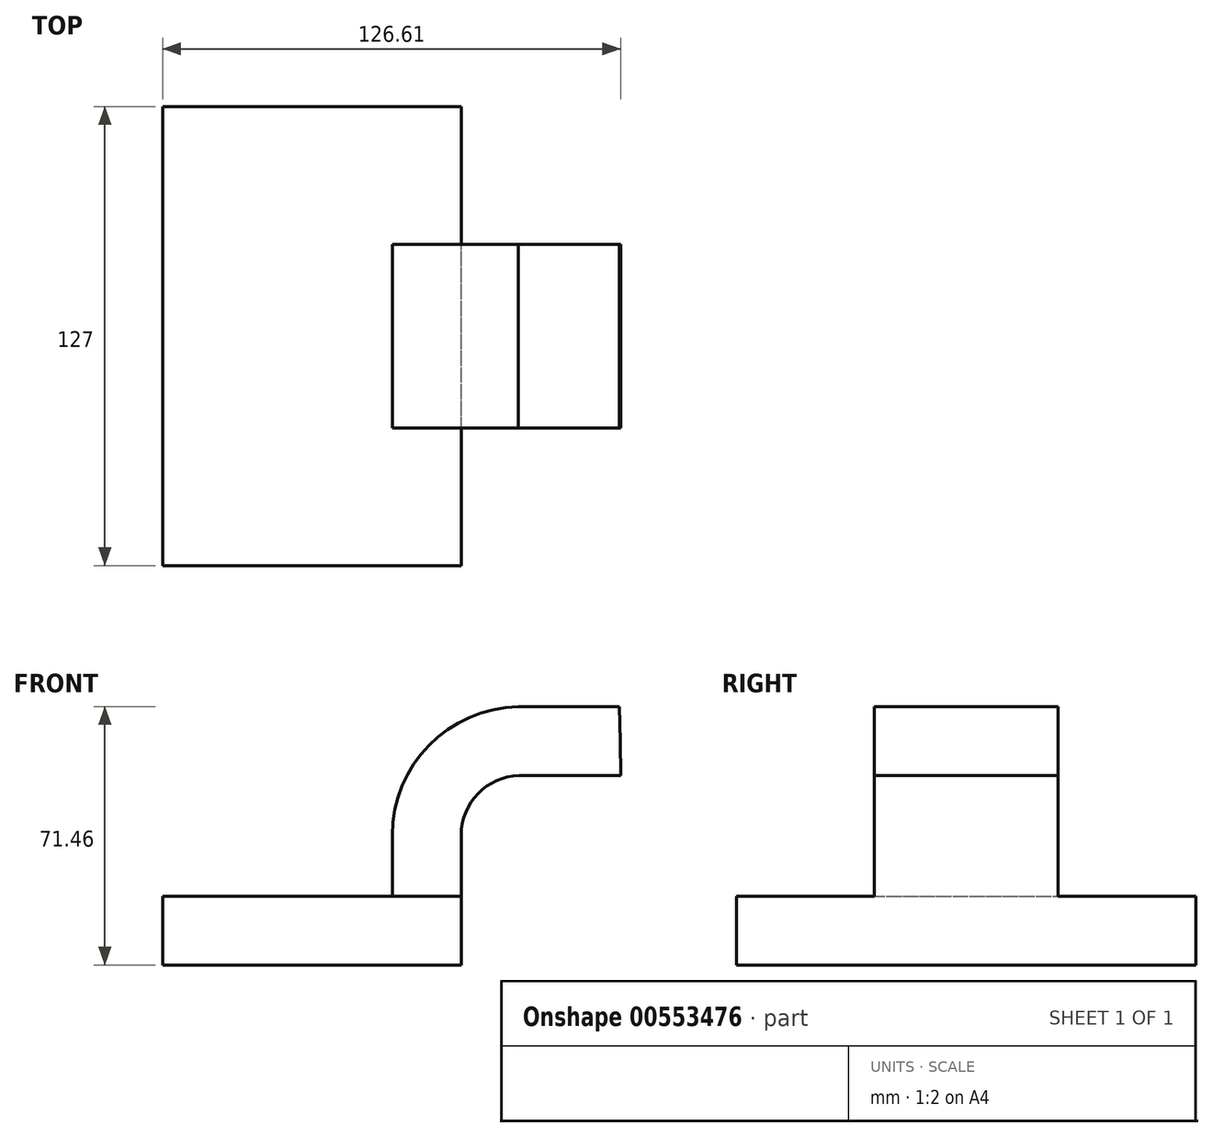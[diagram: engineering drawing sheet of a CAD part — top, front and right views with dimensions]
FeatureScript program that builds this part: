
annotation { "Feature Type Name" : "Feature", "Feature Type Description" : "" }
export const myFeature = defineFeature(function(context is Context, id is Id, definition is map)
    precondition{}
    {
        {
            var Q0;
            Q0=qCreatedBy(makeId("Front.planeOp"),FACE);
            var sketch = newSketch(context, id + "F0", { "sketchPlane" : qUnion([Q0])});
            skLineSegment(sketch, "E0.bottom", {"start": v(-41.27, -9.53) * mm, "end": v(41.28, -9.53) * mm});
            skLineSegment(sketch, "E0.top", {"start": v(-41.28, 9.53) * mm, "end": v(41.28, 9.53) * mm});
            skLineSegment(sketch, "E0.left", {"start": v(-41.28, -9.53) * mm, "end": v(-41.28, 9.53) * mm});
            skLineSegment(sketch, "E0.right", {"start": v(41.28, -9.53) * mm, "end": v(41.28, 9.53) * mm});
            skPoint(sketch, "E0.middle", {"position": v(0, 0) * mm});
            skLineSegment(sketch, "E1", {"start": v(41.27, 9.53) * mm, "end": v(41.27, 26.37) * mm});
            skArc(sketch, "E2", {"start": v(41.27, 26.37) * mm, "mid": v(45.94, 37.87) * mm, "end": v(57.29, 42.88) * mm});
            skLineSegment(sketch, "E3", {"start": v(57.29, 42.88) * mm, "end": v(85.39, 42.88) * mm});
            skLineSegment(sketch, "E4.0", {"start": v(57.05, 61.93) * mm, "end": v(85.03, 61.93) * mm});
            skArc(sketch, "E4.1", {"start": v(22.22, 26.37) * mm, "mid": v(32.38, 51.26) * mm, "end": v(57.05, 61.93) * mm});
            skLineSegment(sketch, "E4.2", {"start": v(22.22, 9.53) * mm, "end": v(22.22, 26.37) * mm});
            skFitSpline(sketch, "E5", {"points": [v(-41.27, 9.53) * mm, v(57.05, 61.93) * mm], "startDerivative": vector(2.15, 108.85) * mm, "endDerivative": vector(132.06, 1.4) * mm});
            skLineSegment(sketch, "E6", {"start": v(85.03, 61.93) * mm, "end": v(85.39, 42.88) * mm});
            skLineSegment(sketch, "E7.bottom", {"start": v(110.6, 38.11) * mm, "end": v(59.8, 38.11) * mm});
            skLineSegment(sketch, "E7.top", {"start": v(110.6, 66.69) * mm, "end": v(59.8, 66.69) * mm});
            skLineSegment(sketch, "E7.left", {"start": v(110.6, 38.11) * mm, "end": v(110.6, 66.69) * mm});
            skLineSegment(sketch, "E7.right", {"start": v(59.8, 38.11) * mm, "end": v(59.8, 66.69) * mm});
            skPoint(sketch, "E7.middle", {"position": v(85.2, 52.4) * mm});
            skLineSegment(sketch, "E8", {"start": v(85.03, 66.69) * mm, "end": v(85.39, 38.11) * mm});
            skPoint(sketch, "E8.startSnap0", {"position": v(85.2, 66.69) * mm});
            skSolve(sketch);
        }
        {
            var Q0;
            Q0=makeQuery(id+"F0.imprint","IMPRINT",FACE,{"disambiguationData":[TD([[makeQuery(id+"F0.imprint","IMPRINT",EDGE,{"derivedFrom":sQuery(id+"F0.wireOp",EDGE,"E0.bottom")}),1.0]])]});
            extrude(context, id + "F1", {"entities" : qUnion([Q0]), "endBound" : BoundingType.SYMMETRIC, "depth" : 127 * mm, "offsetDistance" : 25.4 * mm});
        }
        {
            var Q0;
            Q0=makeQuery(id+"F0.imprint","IMPRINT",FACE,{"disambiguationData":[TD([[makeQuery(id+"F0.imprint","IMPRINT",EDGE,{"derivedFrom":sQuery(id+"F0.wireOp",EDGE,"E4.1")}),1.0]])]});
            extrude(context, id + "F2", {"entities" : qUnion([Q0]), "operationType" : NewBodyOperationType.ADD, "depth" : 15.88 * mm, "offsetDistance" : 25.4 * mm});
        }
        {
            var Q0;
            {var subQ1=sQuery(id+"F0.wireOp",EDGE,"E1");Q0=makeQuery(id+"F0.imprint","IMPRINT",FACE,{"disambiguationData":[TD([[makeQuery(id+"F0.imprint","IMPRINT",EDGE,{"derivedFrom":subQ1}),1.0]])]});}
            var Q1;
            {var subQ5=sQuery(id+"F0.wireOp",EDGE,"E3");var subQ7=sQuery(id+"F0.wireOp",EDGE,"E7.right");var subQ9=makeQuery(id+"F0.imprint","INTERSECT",VERTEX,{"derivedFrom":[subQ5,subQ7]});Q1=makeQuery(id+"F0.imprint","IMPRINT",FACE,{"disambiguationData":[TD([[makeQuery(id+"F0.imprint","IMPRINT",EDGE,{"disambiguationData":[TD([[subQ9,-1.0]])],"derivedFrom":subQ5}),1.0]])]});}
            extrude(context, id + "F3", {"entities" : qUnion([Q0, Q1]), "operationType" : NewBodyOperationType.ADD, "endBound" : BoundingType.SYMMETRIC, "depth" : 50.8 * mm, "offsetDistance" : 25.4 * mm});
        }
    });
